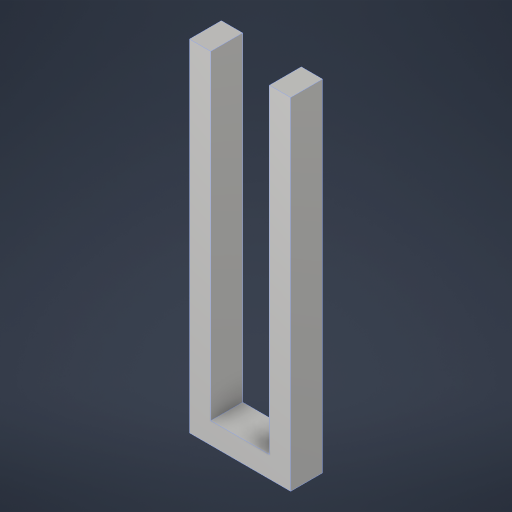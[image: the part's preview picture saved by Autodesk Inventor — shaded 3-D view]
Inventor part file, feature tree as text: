
AUTODESK INVENTOR PART (.ipt)
format: ipt  version: 2024.2 (Build 282272000, 272)  size: 179,200 bytes
history: native  units: in
note: dims shown in document units (in); Inventor stores cm internally (conversion verified against a paired STEP export)
features: extrude x2, sketch x2, projected_geometry x1
ambient origin geometry x8: Origin, YZ Plane, XZ Plane, XY Plane, X Axis, Y Axis, Z Axis, Center Point
bodies: Solid1 (feature_tree)
feature tree (5):
  extrude  "Extrusion1"  Depth=32.0in
  extrude  "Extrusion2"  Depth=2.0in
  sketch  "Sketch1"  dims[d0=9.5in d1=32.0in]
  sketch  "Sketch2"  dims[d2=3.0in d3=0.0in d4=2.0in d5=2.0in d6=2.0in d7=1.0in d8=0.0in]
  projected_geometry  "Project Cut Edges1"
